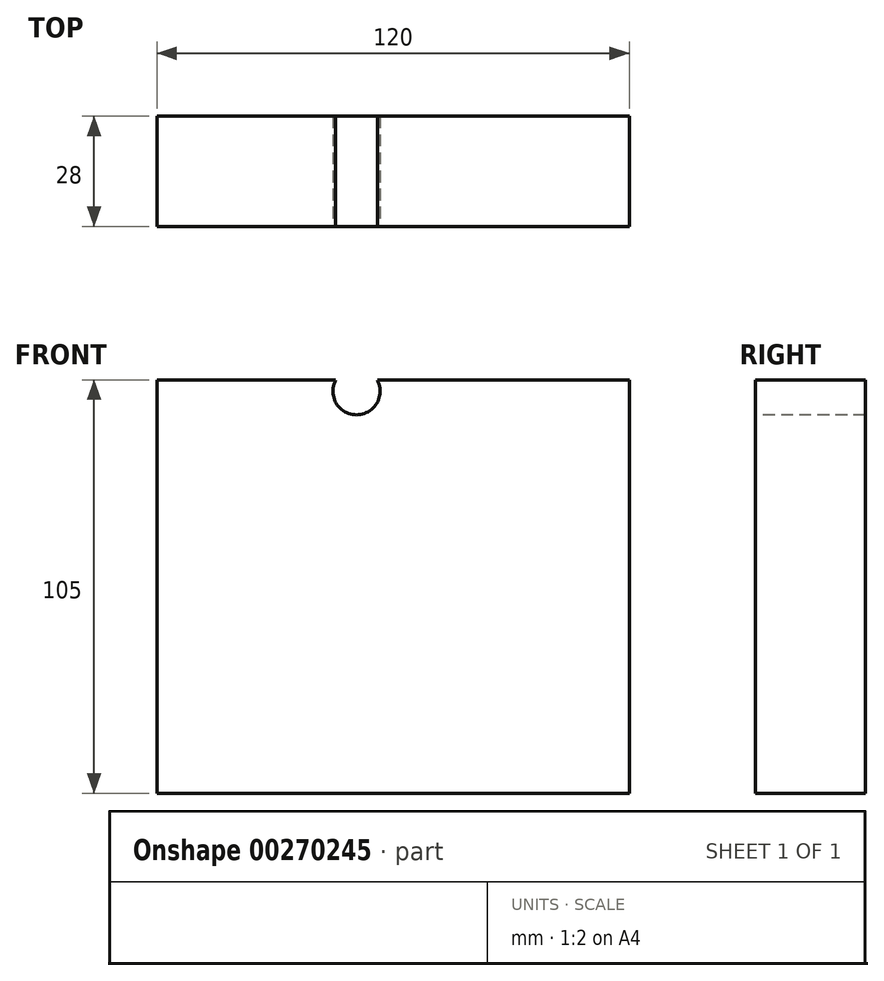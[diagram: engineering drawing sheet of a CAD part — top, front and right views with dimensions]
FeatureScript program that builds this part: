
annotation { "Feature Type Name" : "Feature", "Feature Type Description" : "" }
export const myFeature = defineFeature(function(context is Context, id is Id, definition is map)
    precondition{}
    {
        {
            var Q0;
            Q0=qCreatedBy(makeId("Front.planeOp"),FACE);
            var sketch = newSketch(context, id + "F0", { "sketchPlane" : qUnion([Q0])});
            skLineSegment(sketch, "E0.bottom", {"start": v(-62.94, 63) * mm, "end": v(57.06, 63) * mm});
            skLineSegment(sketch, "E0.top", {"start": v(-62.94, -42) * mm, "end": v(57.06, -42) * mm});
            skLineSegment(sketch, "E0.left", {"start": v(-62.94, 63) * mm, "end": v(-62.94, -42) * mm});
            skLineSegment(sketch, "E0.right", {"start": v(57.06, 63) * mm, "end": v(57.06, -42) * mm});
            skSolve(sketch);
        }
        {
            var Q0;
            Q0=makeQuery(id+"F0.imprint","IMPRINT",FACE,{"disambiguationData":[TD([[makeQuery(id+"F0.imprint","IMPRINT",EDGE,{"derivedFrom":sQuery(id+"F0.wireOp",EDGE,"E0.bottom")}),-1.0]])]});
            extrude(context, id + "F1", {"entities" : qUnion([Q0]), "depth" : 28 * mm});
        }
        {
            var Q0;
            Q0=makeQuery(id+"F1.opExtrude","CAP_FACE",FACE,{"disambiguationData":[OSD([sQuery(id+"F0.wireOp",EDGE,"E0.bottom"),sQuery(id+"F0.wireOp",EDGE,"E0.top"),sQuery(id+"F0.wireOp",EDGE,"E0.left"),sQuery(id+"F0.wireOp",EDGE,"E0.right")])],"isStart":false});
            var sketch = newSketch(context, id + "F2", { "sketchPlane" : qUnion([Q0])});
            skArc(sketch, "E1", {"start": v(-17.51, 63) * mm, "mid": v(-12.23, 54.15) * mm, "end": v(-6.95, 63) * mm});
            skSolve(sketch);
        }
        {
            var Q0;
            Q0=sQuery(id+"F2.wireOp",VERTEX,"E1.center");
            var Q1;
            Q1=makeQuery(id+"F1.opExtrude","SWEPT_BODY",BODY,{"disambiguationData":[OSD([sQuery(id+"F0.wireOp",EDGE,"E0.bottom"),sQuery(id+"F0.wireOp",EDGE,"E0.top"),sQuery(id+"F0.wireOp",EDGE,"E0.left"),sQuery(id+"F0.wireOp",EDGE,"E0.right")])]});
            hole(context, id + "F3", {"style" : HoleStyle.SIMPLE, "endStyle" : HoleEndStyle.THROUGH, "holeDiameter" : 12 * mm, "tappedDepth" : 12 * mm, "tapClearance" : 3, "locations" : qUnion([Q0]), "scope" : qUnion([Q1])});
        }
    });
